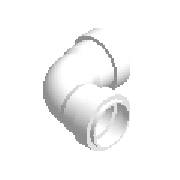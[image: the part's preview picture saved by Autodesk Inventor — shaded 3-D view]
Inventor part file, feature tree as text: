
AUTODESK INVENTOR PART (.ipt)
format: ipt  version: 2023 (Build 270158000, 158)  size: 267,264 bytes
history: native  units: mm (DEFAULTED — no unit token found)
features: other x4, sketch x3, revolve x1
ambient origin geometry x8: Origin, YZ Plane, XZ Plane, XY Plane, X Axis, Y Axis, Z Axis, Center Point
bodies: Solid1 (feature_tree)
feature tree (8):
  sketch  "Sketch1"  dims[d3=90.0deg d0=2.25mm]
  revolve  "Revolution1"  [1 undecoded]
  sketch  "Sketch2"  dims[d1=2.25mm]
  other  "Work Axis31"
  other  "Work Point21"
  other  "Work Axis32"
  other  "Work Point22"
  sketch  "Sketch3"  dims[d2=2.25mm d4=2.7mm d5=2.25mm d6=6.75mm d7=40.3mm d8=18.0mm d9=18.0mm d10=0.0mm d11=6.3mm d12=40.0mm d13=3.0mm d14=2.7mm d15=32.0mm d16=32.0mm d17=40.3mm d18=2.25mm d19=2.25mm d20=2.25mm d21=2.25mm d22=4.5mm d23=2.7mm d24=3.0mm d25=40.0mm d26=6.3mm d27=18.0mm d28=18.0mm d29=32.0mm d30=32.0mm d31=2.7mm d206=90.0deg d207=0.0mm]
note: 1 required parameter value undecoded (feature->parameter linkage not recoverable at this tier; creation-order binding heuristic only, values carry confidence <= 0.55)
